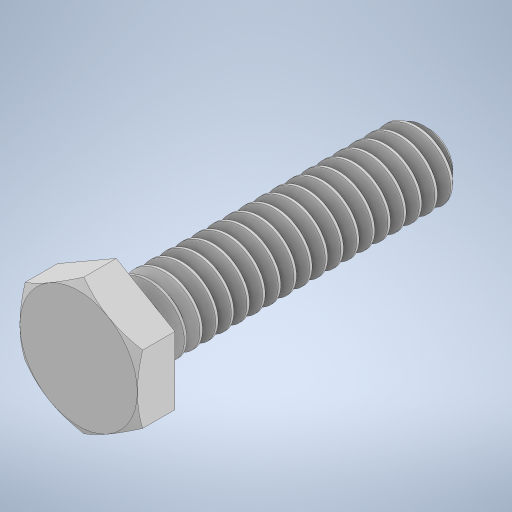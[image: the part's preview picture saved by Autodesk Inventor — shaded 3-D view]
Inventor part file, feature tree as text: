
AUTODESK INVENTOR PART (.ipt)
format: ipt  version: 2024 (Build 280153000, 153)  size: 700,928 bytes
history: native  units: in
note: dims shown in document units (in); Inventor stores cm internally (conversion verified against a paired STEP export)
features: extrude x1
ambient origin geometry x8: Origin, YZ Plane, XZ Plane, XY Plane, X Axis, Y Axis, Z Axis, Center Point
bodies: Solid1 (feature_tree)
feature tree (1):
  extrude  "Extrude13"  [1 undecoded]
note: 1 required parameter value undecoded (feature->parameter linkage not recoverable at this tier; creation-order binding heuristic only, values carry confidence <= 0.55)
